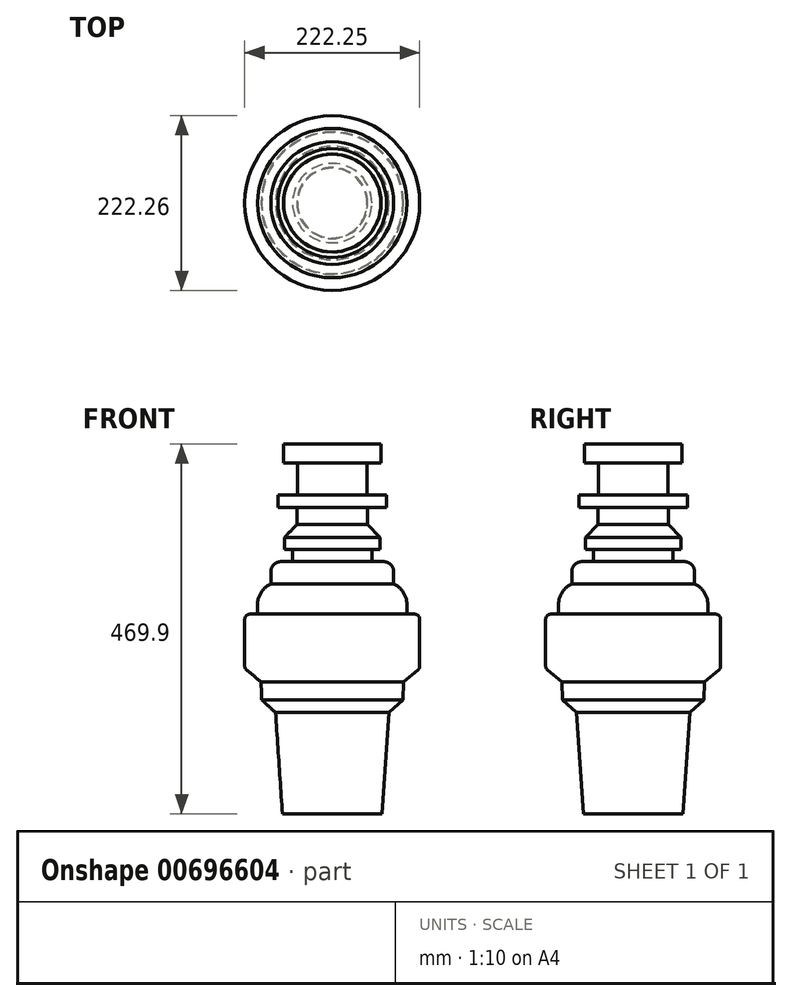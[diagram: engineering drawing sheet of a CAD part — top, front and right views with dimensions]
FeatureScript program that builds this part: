
annotation { "Feature Type Name" : "Feature", "Feature Type Description" : "" }
export const myFeature = defineFeature(function(context is Context, id is Id, definition is map)
    precondition{}
    {
        {
            var Q0;
            Q0=qCreatedBy(makeId("Front.planeOp"),FACE);
            var sketch = newSketch(context, id + "F0", { "sketchPlane" : qUnion([Q0])});
            skLineSegment(sketch, "E0", {"start": v(110.02, -259.23) * mm, "end": v(110.02, 210.67) * mm});
            skLineSegment(sketch, "E1", {"start": v(110.02, 210.67) * mm, "end": v(48.06, 210.67) * mm});
            skLineSegment(sketch, "E2", {"start": v(48.06, 210.67) * mm, "end": v(48.06, 186.44) * mm});
            skLineSegment(sketch, "E3", {"start": v(48.06, 186.44) * mm, "end": v(65.7, 186.44) * mm});
            skLineSegment(sketch, "E4", {"start": v(65.7, 186.44) * mm, "end": v(65.7, 146.12) * mm});
            skLineSegment(sketch, "E5", {"start": v(65.7, 146.12) * mm, "end": v(40.86, 146.12) * mm});
            skLineSegment(sketch, "E6", {"start": v(40.86, 146.12) * mm, "end": v(40.86, 130) * mm});
            skLineSegment(sketch, "E7", {"start": v(40.86, 130) * mm, "end": v(64.99, 130) * mm});
            skLineSegment(sketch, "E8", {"start": v(64.99, 130) * mm, "end": v(64.99, 108.32) * mm});
            skLineSegment(sketch, "E9", {"start": v(64.99, 108.32) * mm, "end": v(49.1, 91.87) * mm});
            skLineSegment(sketch, "E10", {"start": v(49.1, 91.87) * mm, "end": v(49.1, 76.56) * mm});
            skLineSegment(sketch, "E11", {"start": v(49.1, 76.56) * mm, "end": v(59.57, 76.56) * mm});
            skLineSegment(sketch, "E12", {"start": v(59.57, 76.56) * mm, "end": v(59.57, 61.28) * mm});
            skLineSegment(sketch, "E13", {"start": v(15.13, 33.1) * mm, "end": v(15.13, -5.47) * mm});
            skLineSegment(sketch, "E14", {"start": v(15.13, -5.47) * mm, "end": v(-1.1, -5.47) * mm});
            skLineSegment(sketch, "E15", {"start": v(-1.1, -5.47) * mm, "end": v(-1.1, -74.5) * mm});
            skLineSegment(sketch, "E16", {"start": v(-1.1, -74.5) * mm, "end": v(19.6, -91.37) * mm});
            skLineSegment(sketch, "E17", {"start": v(19.6, -91.37) * mm, "end": v(20.37, -114.38) * mm});
            skLineSegment(sketch, "E18", {"start": v(20.37, -114.38) * mm, "end": v(38, -130.49) * mm});
            skLineSegment(sketch, "E19", {"start": v(38, -130.49) * mm, "end": v(46.78, -259.23) * mm});
            skLineSegment(sketch, "E20", {"start": v(46.78, -259.23) * mm, "end": v(110.02, -259.23) * mm});
            skLineSegment(sketch, "E21", {"start": v(15.13, 33.1) * mm, "end": v(32.03, 33.1) * mm});
            skLineSegment(sketch, "E22", {"start": v(32.03, 33.1) * mm, "end": v(32.03, 61.28) * mm});
            skLineSegment(sketch, "E23", {"start": v(32.03, 61.28) * mm, "end": v(59.57, 61.28) * mm});
            skSolve(sketch);
        }
        {
            var Q0;
            Q0 = qSketchRegion(id + "F0", true);
            var Q1;
            Q1=sQuery(id+"F0.wireOp",EDGE,"E0");
            revolve(context, id + "F1", {"entities" : qUnion([Q0]), "axis" : qUnion([Q1]), "revolveType" : RevolveType.FULL});
        }
        {
            var Q0;
            Q0=makeQuery(id+"F1.opRevolve","SWEPT_EDGE",EDGE,{"disambiguationData":[OSD([sQuery(id+"F0.wireOp",EDGE,"E22"),sQuery(id+"F0.wireOp",EDGE,"E23")])]});
            fillet(context, id + "F2", {"entities" : qUnion([Q0]), "radius" : 12.7 * mm, "tangentPropagation" : true, "allowEdgeOverflow" : false});
        }
        {
            var Q0;
            Q0=makeQuery(id+"F1.opRevolve","SWEPT_EDGE",EDGE,{"disambiguationData":[OSD([sQuery(id+"F0.wireOp",EDGE,"E13"),sQuery(id+"F0.wireOp",EDGE,"E21")])]});
            fillet(context, id + "F3", {"entities" : qUnion([Q0]), "radius" : 29.43 * mm, "tangentPropagation" : true, "allowEdgeOverflow" : false});
        }
        {
            var Q0;
            Q0=makeQuery(id+"F1.opRevolve","SWEPT_EDGE",EDGE,{"disambiguationData":[OSD([sQuery(id+"F0.wireOp",EDGE,"E14"),sQuery(id+"F0.wireOp",EDGE,"E15")])]});
            var Q1;
            Q1=makeQuery(id+"F1.opRevolve","SWEPT_EDGE",EDGE,{"disambiguationData":[OSD([sQuery(id+"F0.wireOp",EDGE,"E15"),sQuery(id+"F0.wireOp",EDGE,"E16")])]});
            fillet(context, id + "F4", {"entities" : qUnion([Q0, Q1]), "radius" : 6.35 * mm, "tangentPropagation" : true, "allowEdgeOverflow" : false});
        }
    });
